# Revit family: Reece_Mirror_Kado_Neue_Mirror Cabinet_900 x 1050 mm
name_source: partatom
category: Casework
revit_build: Autodesk Revit 2018 (Build: 20190510_1515(x64)
units: mm (PartAtom-declared; Revit-internal decimal feet)

## family parameters
Always vertical = Yes
Cut with Voids When Loaded = Yes
Room Calculation Point = Yes
Shared = Yes
Work Plane-Based = Yes

## types (1)
- 902 mm x 1051 mm x 120 mm_2 Doors
    Default Elevation = 0 mm  [stored 0 ft]
    Description = Kado Neue Arch 900 x 1050mm 2 Door Mirrored Shave Cabinet
    Disclaimer = THIS FILE IS THE PROPERTY OF THE REECE GROUP. IT MAY NOT BE REPRODUCED, REVERSE-ENGINEERED OR MODIFIED. ANY REPUBLICATION, TRANSMISSION OR DISTRIBUTION FOR THE PURPOSE OF COMMERCIALLY EXPLOITING THE FILES IS PROHIBITED.
    Finish = Please refer to Colour, Finish and Material Variations Document for more information.
    Keynote = Product #2351625, Reece_Mirror_Kado_Neue_Mirror Cabinet_900 x 1050 mm - 902 mm x 1051 mm x 120 mm_2 Doors
    Manufacturer = Kado
    Model = Neue
    Reece_Detail_Disclaimer = THIS FILE IS THE PROPERTY OF THE REECE GROUP. IT MAY NOT BE REPRODUCED, REVERSE-ENGINEERED OR MODIFIED. ANY REPUBLICATION, TRANSMISSION OR DISTRIBUTION FOR THE PURPOSE OF COMMERCIALLY EXPLOITING THE FILES IS PROHIBITED.
    Reece_Material_Cabinet = Reece_Solid_Surface_Matte_White
    Reece_Material_Main = Reece_Glass_Mirror
    Reece_Material_Secondary = Reece_Plastic_White
    Reece_Overall_Depth = 120 mm  [stored 0.393701 ft]
    Reece_Overall_Height = 1051 mm  [stored 3.44816 ft]
    Reece_Overall_Width = 902 mm  [stored 2.95932 ft]
    Reece_Product_Brand = Kado
    Reece_Product_Description = Kado Neue Arch 900 x 1050mm 2 Door Mirrored Shave Cabinet
    Reece_Product_Finishes_Web Page = https://digitalassets.reecegroup.com.au
    Reece_Product_Mount = Wall Mounted
    Reece_Product_Number = 2351625
    Reece_Product_Sub Brand = Neue
    Reece_Product_Type = Mirror
    Reece_Product_Web Page = https://www.reece.com.au
    Type Comments = Mirror
    URL = https://www.reece.com.au

note: [stored X ft] marks values corroborated as IEEE doubles in the binary element streams (Revit-internal decimal feet)

## geometry (parser evidence)
native form markers: Sweep x6
no freeform markers — native parametric forms only
